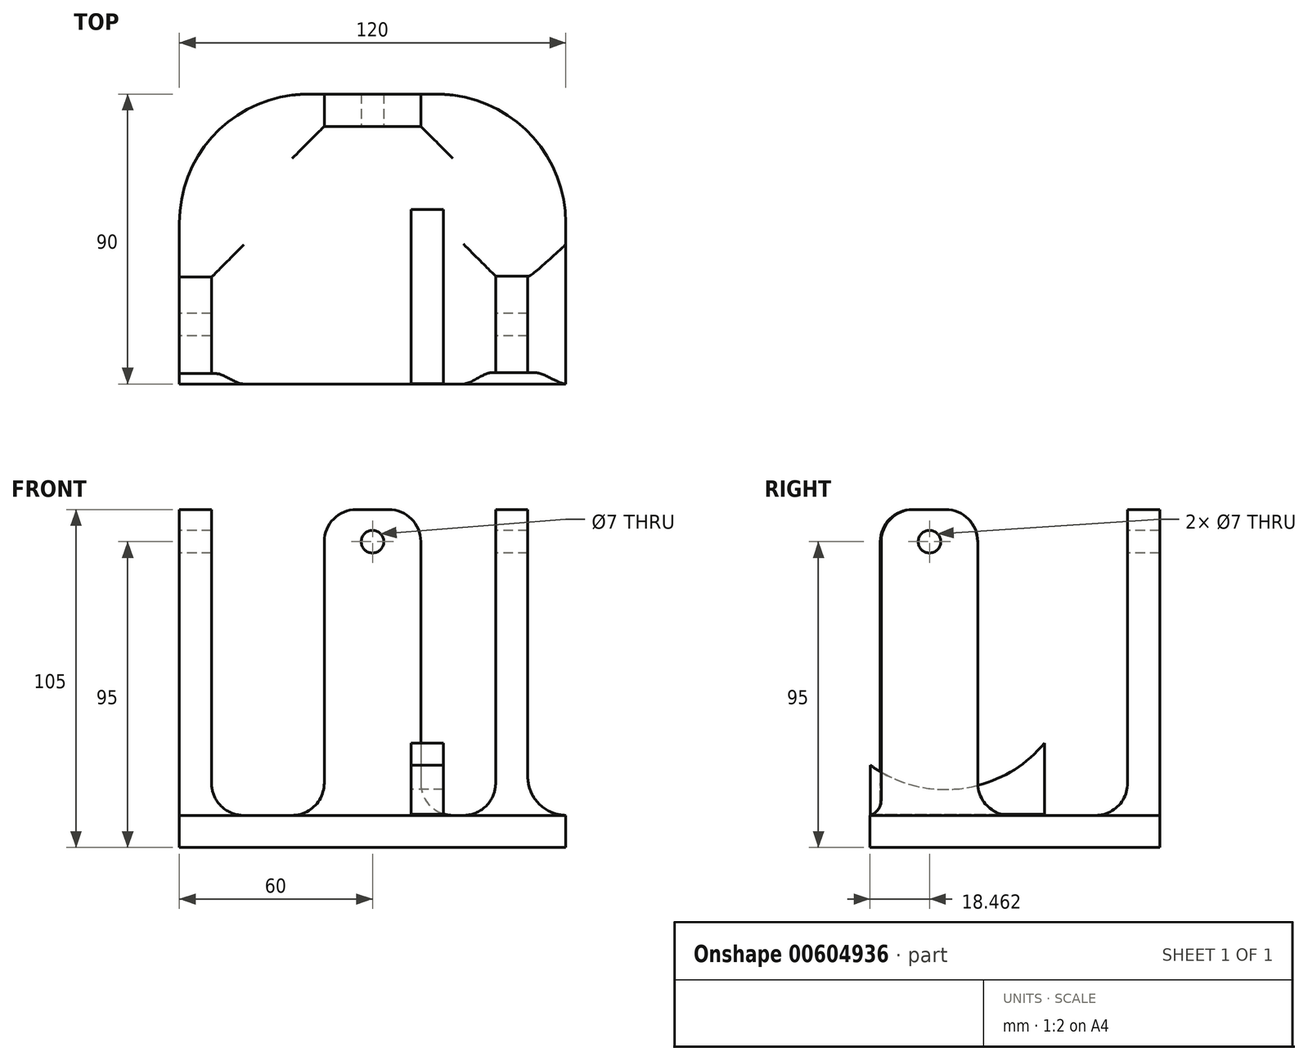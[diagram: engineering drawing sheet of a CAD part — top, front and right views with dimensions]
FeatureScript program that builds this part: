
annotation { "Feature Type Name" : "Feature", "Feature Type Description" : "" }
export const myFeature = defineFeature(function(context is Context, id is Id, definition is map)
    precondition{}
    {
        {
            var Q0;
            Q0=qCreatedBy(makeId("Top.planeOp"),FACE);
            var sketch = newSketch(context, id + "F0", { "sketchPlane" : qUnion([Q0])});
            skLineSegment(sketch, "E0.bottom", {"start": v(-20, 45) * mm, "end": v(20, 45) * mm});
            skLineSegment(sketch, "E0.top", {"start": v(-60, -45) * mm, "end": v(60, -45) * mm});
            skLineSegment(sketch, "E0.left", {"start": v(-60, 5) * mm, "end": v(-60, -45) * mm});
            skLineSegment(sketch, "E0.right", {"start": v(60, 5) * mm, "end": v(60, -45) * mm});
            skPoint(sketch, "E0.middle", {"position": v(0, 0) * mm});
            skPoint(sketch, "E1.visualSharp", {"position": v(-60, 45) * mm});
            skArc(sketch, "E1.filletArc", {"start": v(-20, 45) * mm, "mid": v(-48.28, 33.28) * mm, "end": v(-60, 5) * mm});
            skPoint(sketch, "E2.visualSharp", {"position": v(60, 45) * mm});
            skArc(sketch, "E2.filletArc", {"start": v(60, 5) * mm, "mid": v(48.28, 33.28) * mm, "end": v(20, 45) * mm});
            skSolve(sketch);
        }
        {
            var Q0;
            Q0=makeQuery(id+"F0.imprint","IMPRINT",FACE,{"disambiguationData":[TD([[makeQuery(id+"F0.imprint","IMPRINT",EDGE,{"derivedFrom":sQuery(id+"F0.wireOp",EDGE,"E0.bottom")}),-1.0]])]});
            extrude(context, id + "F1", {"entities" : qUnion([Q0]), "depth" : 10 * mm, "offsetDistance" : 25 * mm});
        }
        {
            var Q0;
            Q0=makeQuery(id+"F1.opExtrude","CAP_FACE",FACE,{"disambiguationData":[OSD([sQuery(id+"F0.wireOp",EDGE,"E0.bottom"),sQuery(id+"F0.wireOp",EDGE,"E0.top"),sQuery(id+"F0.wireOp",EDGE,"E0.left"),sQuery(id+"F0.wireOp",EDGE,"E0.right"),sQuery(id+"F0.wireOp",EDGE,"E1.filletArc"),sQuery(id+"F0.wireOp",EDGE,"E2.filletArc")])],"isStart":false});
            var sketch = newSketch(context, id + "F2", { "sketchPlane" : qUnion([Q0])});
            skSolve(sketch);
        }
        {
            var Q0;
            Q0=qCreatedBy(makeId("Top.planeOp"),FACE);
            var sketch = newSketch(context, id + "F3", { "sketchPlane" : qUnion([Q0])});
            skLineSegment(sketch, "E3.bottom", {"start": v(-60, -41.81) * mm, "end": v(-50, -41.81) * mm});
            skLineSegment(sketch, "E3.top", {"start": v(-60, -11.81) * mm, "end": v(-50, -11.81) * mm});
            skLineSegment(sketch, "E3.left", {"start": v(-60, -41.81) * mm, "end": v(-60, -11.81) * mm});
            skLineSegment(sketch, "E3.right", {"start": v(-50, -41.81) * mm, "end": v(-50, -11.81) * mm});
            skLineSegment(sketch, "E4.bottom", {"start": v(38.23, -41.54) * mm, "end": v(48.23, -41.54) * mm});
            skLineSegment(sketch, "E4.top", {"start": v(38.23, -11.54) * mm, "end": v(48.23, -11.54) * mm});
            skLineSegment(sketch, "E4.left", {"start": v(38.23, -41.54) * mm, "end": v(38.23, -11.54) * mm});
            skLineSegment(sketch, "E4.right", {"start": v(48.23, -41.54) * mm, "end": v(48.23, -11.54) * mm});
            skLineSegment(sketch, "E5.bottom", {"start": v(-15, 45) * mm, "end": v(15, 45) * mm});
            skLineSegment(sketch, "E5.top", {"start": v(-15, 35) * mm, "end": v(15, 35) * mm});
            skLineSegment(sketch, "E5.left", {"start": v(-15, 45) * mm, "end": v(-15, 35) * mm});
            skLineSegment(sketch, "E5.right", {"start": v(15, 45) * mm, "end": v(15, 35) * mm});
            skSolve(sketch);
        }
        {
            var Q0;
            Q0 = qSketchRegion(id + "F3", true);
            extrude(context, id + "F4", {"entities" : qUnion([Q0]), "operationType" : NewBodyOperationType.ADD, "depth" : 25 * mm, "offsetDistance" : 25 * mm});
        }
        {
            var Q0;
            Q0 = qSketchRegion(id + "F3", true);
            var Q1;
            Q1=makeQuery(id+"F4.opExtrude","CAP_FACE",FACE,{"disambiguationData":[OSD([sQuery(id+"F3.wireOp",EDGE,"E3.bottom"),sQuery(id+"F3.wireOp",EDGE,"E3.top"),sQuery(id+"F3.wireOp",EDGE,"E3.left"),sQuery(id+"F3.wireOp",EDGE,"E3.right")])],"isStart":false});
            var Q2;
            Q2=makeQuery(id+"F4.opExtrude","CAP_FACE",FACE,{"disambiguationData":[OSD([sQuery(id+"F3.wireOp",EDGE,"E5.bottom"),sQuery(id+"F3.wireOp",EDGE,"E5.top"),sQuery(id+"F3.wireOp",EDGE,"E5.left"),sQuery(id+"F3.wireOp",EDGE,"E5.right")])],"isStart":false});
            var Q3;
            Q3=makeQuery(id+"F4.opExtrude","CAP_FACE",FACE,{"disambiguationData":[OSD([sQuery(id+"F3.wireOp",EDGE,"E4.bottom"),sQuery(id+"F3.wireOp",EDGE,"E4.top"),sQuery(id+"F3.wireOp",EDGE,"E4.left"),sQuery(id+"F3.wireOp",EDGE,"E4.right")])],"isStart":false});
            extrude(context, id + "F5", {"entities" : qUnion([Q0, Q1, Q2, Q3]), "operationType" : NewBodyOperationType.ADD, "depth" : 80 * mm, "offsetDistance" : 25 * mm});
        }
        {
            var Q0;
            {var subQ0=sQuery(id+"F3.wireOp",EDGE,"E4.bottom");Q0=makeQuery(id+"F5.opExtrude","CAP_EDGE",EDGE,{"disambiguationData":[OSD([subQ0]),TDD([makeQuery(id+"F4.opExtrude","CAP_EDGE",EDGE,{"disambiguationData":[OSD([subQ0])],"isStart":false})])],"isStart":false});}
            var Q1;
            {var subQ0=sQuery(id+"F3.wireOp",EDGE,"E4.top");Q1=makeQuery(id+"F5.opExtrude","CAP_EDGE",EDGE,{"disambiguationData":[OSD([subQ0]),TDD([makeQuery(id+"F4.opExtrude","CAP_EDGE",EDGE,{"disambiguationData":[OSD([subQ0])],"isStart":false})])],"isStart":false});}
            fillet(context, id + "F6", {"entities" : qUnion([Q0, Q1]), "radius" : 10 * mm, "tangentPropagation" : true, "allowEdgeOverflow" : false});
        }
        {
            var Q0;
            {var subQ0=sQuery(id+"F3.wireOp",EDGE,"E5.right");Q0=makeQuery(id+"F5.opExtrude","CAP_EDGE",EDGE,{"disambiguationData":[OSD([subQ0]),TDD([makeQuery(id+"F4.opExtrude","CAP_EDGE",EDGE,{"disambiguationData":[OSD([subQ0])],"isStart":false})])],"isStart":false});}
            fillet(context, id + "F7", {"entities" : qUnion([Q0]), "radius" : 10 * mm, "tangentPropagation" : true, "allowEdgeOverflow" : false});
        }
        {
            var Q0;
            {var subQ0=sQuery(id+"F3.wireOp",EDGE,"E5.left");Q0=makeQuery(id+"F5.opExtrude","CAP_EDGE",EDGE,{"disambiguationData":[OSD([subQ0]),TDD([makeQuery(id+"F4.opExtrude","CAP_EDGE",EDGE,{"disambiguationData":[OSD([subQ0])],"isStart":false})])],"isStart":false});}
            fillet(context, id + "F8", {"entities" : qUnion([Q0]), "radius" : 10 * mm, "tangentPropagation" : true, "allowEdgeOverflow" : false});
        }
        {
            var Q0;
            {var subQ0=sQuery(id+"F3.wireOp",EDGE,"E3.top");Q0=makeQuery(id+"F5.opExtrude","CAP_EDGE",EDGE,{"disambiguationData":[OSD([subQ0]),TDD([makeQuery(id+"F4.opExtrude","CAP_EDGE",EDGE,{"disambiguationData":[OSD([subQ0])],"isStart":false})])],"isStart":false});}
            var Q1;
            {var subQ0=sQuery(id+"F3.wireOp",EDGE,"E3.bottom");Q1=makeQuery(id+"F5.opExtrude","CAP_EDGE",EDGE,{"disambiguationData":[OSD([subQ0]),TDD([makeQuery(id+"F4.opExtrude","CAP_EDGE",EDGE,{"disambiguationData":[OSD([subQ0])],"isStart":false})])],"isStart":false});}
            fillet(context, id + "F9", {"entities" : qUnion([Q0, Q1]), "radius" : 10 * mm, "tangentPropagation" : true, "allowEdgeOverflow" : false});
        }
        {
            var Q0;
            {var subQ0=sQuery(id+"F3.wireOp",EDGE,"E5.top");Q0=makeQuery(id+"F5.boolean.opBoolean","MERGE",FACE,{"derivedFrom":[makeQuery(id+"F4.opExtrude","SWEPT_FACE",FACE,{"disambiguationData":[OSD([subQ0])]}),makeQuery(id+"F5.opExtrude","SWEPT_FACE",FACE,{"disambiguationData":[OSD([subQ0]),TDD([makeQuery(id+"F3.imprint","IMPRINT",EDGE,{"derivedFrom":subQ0})])]}),makeQuery(id+"F5.opExtrude","SWEPT_FACE",FACE,{"disambiguationData":[OSD([subQ0]),TDD([makeQuery(id+"F4.opExtrude","CAP_EDGE",EDGE,{"disambiguationData":[OSD([subQ0])],"isStart":false})])]})]});}
            var sketch = newSketch(context, id + "F10", { "sketchPlane" : qUnion([Q0])});
            skCircle(sketch, "E6", {"center": v(0, 95) * mm, "radius": 3.5 * mm});
            skSolve(sketch);
        }
        {
            var Q0;
            Q0=sQuery(id+"F10.wireOp",VERTEX,"E6.center");
            var Q1;
            Q1=makeQuery(id+"F1.opExtrude","SWEPT_BODY",BODY,{"disambiguationData":[OSD([sQuery(id+"F0.wireOp",EDGE,"E0.bottom"),sQuery(id+"F0.wireOp",EDGE,"E0.top"),sQuery(id+"F0.wireOp",EDGE,"E0.left"),sQuery(id+"F0.wireOp",EDGE,"E0.right"),sQuery(id+"F0.wireOp",EDGE,"E1.filletArc"),sQuery(id+"F0.wireOp",EDGE,"E2.filletArc")])]});
            hole(context, id + "F11", {"style" : HoleStyle.SIMPLE, "endStyle" : HoleEndStyle.THROUGH, "holeDiameter" : 7 * mm, "majorDiameter" : 5 * mm, "isTappedThrough" : true, "tappedDepth" : 12 * mm, "tapClearance" : 3, "locations" : qUnion([Q0]), "scope" : qUnion([Q1])});
        }
        {
            var Q0;
            {var subQ0=sQuery(id+"F3.wireOp",EDGE,"E3.left");Q0=makeQuery(id+"F5.boolean.opBoolean","MERGE",FACE,{"derivedFrom":[makeQuery(id+"F4.boolean.opBoolean","MERGE",FACE,{"derivedFrom":[makeQuery(id+"F1.opExtrude","SWEPT_FACE",FACE,{"disambiguationData":[OSD([sQuery(id+"F0.wireOp",EDGE,"E0.left")])]}),makeQuery(id+"F4.opExtrude","SWEPT_FACE",FACE,{"disambiguationData":[OSD([subQ0])]})]}),makeQuery(id+"F5.opExtrude","SWEPT_FACE",FACE,{"disambiguationData":[OSD([subQ0]),TDD([makeQuery(id+"F3.imprint","IMPRINT",EDGE,{"derivedFrom":subQ0})])]}),makeQuery(id+"F5.opExtrude","SWEPT_FACE",FACE,{"disambiguationData":[OSD([subQ0]),TDD([makeQuery(id+"F4.opExtrude","CAP_EDGE",EDGE,{"disambiguationData":[OSD([subQ0])],"isStart":false})])]})]});}
            var sketch = newSketch(context, id + "F12", { "sketchPlane" : qUnion([Q0])});
            skCircle(sketch, "E7", {"center": v(26.54, 95) * mm, "radius": 3.5 * mm});
            skSolve(sketch);
        }
        {
            var Q0;
            Q0=sQuery(id+"F12.wireOp",VERTEX,"E7.center");
            var Q1;
            Q1=makeQuery(id+"F1.opExtrude","SWEPT_BODY",BODY,{"disambiguationData":[OSD([sQuery(id+"F0.wireOp",EDGE,"E0.bottom"),sQuery(id+"F0.wireOp",EDGE,"E0.top"),sQuery(id+"F0.wireOp",EDGE,"E0.left"),sQuery(id+"F0.wireOp",EDGE,"E0.right"),sQuery(id+"F0.wireOp",EDGE,"E1.filletArc"),sQuery(id+"F0.wireOp",EDGE,"E2.filletArc")])]});
            hole(context, id + "F13", {"style" : HoleStyle.SIMPLE, "endStyle" : HoleEndStyle.THROUGH, "holeDiameter" : 7 * mm, "majorDiameter" : 5 * mm, "isTappedThrough" : true, "tappedDepth" : 12 * mm, "tapClearance" : 3, "locations" : qUnion([Q0]), "scope" : qUnion([Q1])});
        }
        {
            var Q0;
            Q0=makeQuery(id+"F4.boolean.opBoolean","INTERSECT",EDGE,{"derivedFrom":[makeQuery(id+"F1.opExtrude","CAP_FACE",FACE,{"disambiguationData":[OSD([sQuery(id+"F0.wireOp",EDGE,"E0.bottom"),sQuery(id+"F0.wireOp",EDGE,"E0.top"),sQuery(id+"F0.wireOp",EDGE,"E0.left"),sQuery(id+"F0.wireOp",EDGE,"E0.right"),sQuery(id+"F0.wireOp",EDGE,"E1.filletArc"),sQuery(id+"F0.wireOp",EDGE,"E2.filletArc")])],"isStart":false}),makeQuery(id+"F4.opExtrude","SWEPT_FACE",FACE,{"disambiguationData":[OSD([sQuery(id+"F3.wireOp",EDGE,"E3.top")])]})]});
            fillet(context, id + "F14", {"entities" : qUnion([Q0]), "radius" : 10 * mm, "tangentPropagation" : true, "allowEdgeOverflow" : false});
        }
        {
            var Q0;
            Q0=makeQuery(id+"F4.boolean.opBoolean","INTERSECT",EDGE,{"derivedFrom":[makeQuery(id+"F1.opExtrude","CAP_FACE",FACE,{"disambiguationData":[OSD([sQuery(id+"F0.wireOp",EDGE,"E0.bottom"),sQuery(id+"F0.wireOp",EDGE,"E0.top"),sQuery(id+"F0.wireOp",EDGE,"E0.left"),sQuery(id+"F0.wireOp",EDGE,"E0.right"),sQuery(id+"F0.wireOp",EDGE,"E1.filletArc"),sQuery(id+"F0.wireOp",EDGE,"E2.filletArc")])],"isStart":false}),makeQuery(id+"F4.opExtrude","SWEPT_FACE",FACE,{"disambiguationData":[OSD([sQuery(id+"F3.wireOp",EDGE,"E5.left")])]})]});
            fillet(context, id + "F15", {"entities" : qUnion([Q0]), "radius" : 10 * mm, "tangentPropagation" : true, "allowEdgeOverflow" : false});
        }
        {
            var Q0;
            Q0=makeQuery(id+"F4.boolean.opBoolean","INTERSECT",EDGE,{"derivedFrom":[makeQuery(id+"F1.opExtrude","CAP_FACE",FACE,{"disambiguationData":[OSD([sQuery(id+"F0.wireOp",EDGE,"E0.bottom"),sQuery(id+"F0.wireOp",EDGE,"E0.top"),sQuery(id+"F0.wireOp",EDGE,"E0.left"),sQuery(id+"F0.wireOp",EDGE,"E0.right"),sQuery(id+"F0.wireOp",EDGE,"E1.filletArc"),sQuery(id+"F0.wireOp",EDGE,"E2.filletArc")])],"isStart":false}),makeQuery(id+"F4.opExtrude","SWEPT_FACE",FACE,{"disambiguationData":[OSD([sQuery(id+"F3.wireOp",EDGE,"E5.right")])]})]});
            var Q1;
            Q1=makeQuery(id+"F4.boolean.opBoolean","INTERSECT",EDGE,{"derivedFrom":[makeQuery(id+"F1.opExtrude","CAP_FACE",FACE,{"disambiguationData":[OSD([sQuery(id+"F0.wireOp",EDGE,"E0.bottom"),sQuery(id+"F0.wireOp",EDGE,"E0.top"),sQuery(id+"F0.wireOp",EDGE,"E0.left"),sQuery(id+"F0.wireOp",EDGE,"E0.right"),sQuery(id+"F0.wireOp",EDGE,"E1.filletArc"),sQuery(id+"F0.wireOp",EDGE,"E2.filletArc")])],"isStart":false}),makeQuery(id+"F4.opExtrude","SWEPT_FACE",FACE,{"disambiguationData":[OSD([sQuery(id+"F3.wireOp",EDGE,"E4.top")])]})]});
            fillet(context, id + "F16", {"entities" : qUnion([Q0, Q1]), "radius" : 10 * mm, "tangentPropagation" : true, "allowEdgeOverflow" : false});
        }
        {
            var Q0;
            Q0=makeQuery(id+"F4.boolean.opBoolean","INTERSECT",EDGE,{"derivedFrom":[makeQuery(id+"F1.opExtrude","CAP_FACE",FACE,{"disambiguationData":[OSD([sQuery(id+"F0.wireOp",EDGE,"E0.bottom"),sQuery(id+"F0.wireOp",EDGE,"E0.top"),sQuery(id+"F0.wireOp",EDGE,"E0.left"),sQuery(id+"F0.wireOp",EDGE,"E0.right"),sQuery(id+"F0.wireOp",EDGE,"E1.filletArc"),sQuery(id+"F0.wireOp",EDGE,"E2.filletArc")])],"isStart":false}),makeQuery(id+"F4.opExtrude","SWEPT_FACE",FACE,{"disambiguationData":[OSD([sQuery(id+"F3.wireOp",EDGE,"E4.right")])]})]});
            fillet(context, id + "F17", {"entities" : qUnion([Q0]), "radius" : 12 * mm, "tangentPropagation" : true, "allowEdgeOverflow" : false});
        }
        {
            var Q0;
            Q0=makeQuery(id+"F4.boolean.opBoolean","INTERSECT",EDGE,{"derivedFrom":[makeQuery(id+"F1.opExtrude","CAP_FACE",FACE,{"disambiguationData":[OSD([sQuery(id+"F0.wireOp",EDGE,"E0.bottom"),sQuery(id+"F0.wireOp",EDGE,"E0.top"),sQuery(id+"F0.wireOp",EDGE,"E0.left"),sQuery(id+"F0.wireOp",EDGE,"E0.right"),sQuery(id+"F0.wireOp",EDGE,"E1.filletArc"),sQuery(id+"F0.wireOp",EDGE,"E2.filletArc")])],"isStart":false}),makeQuery(id+"F4.opExtrude","SWEPT_FACE",FACE,{"disambiguationData":[OSD([sQuery(id+"F3.wireOp",EDGE,"E4.bottom")])]})]});
            fillet(context, id + "F18", {"entities" : qUnion([Q0]), "radius" : 5 * mm, "tangentPropagation" : true, "allowEdgeOverflow" : false});
        }
        {
            var Q0;
            Q0=makeQuery(id+"F4.boolean.opBoolean","INTERSECT",EDGE,{"derivedFrom":[makeQuery(id+"F1.opExtrude","CAP_FACE",FACE,{"disambiguationData":[OSD([sQuery(id+"F0.wireOp",EDGE,"E0.bottom"),sQuery(id+"F0.wireOp",EDGE,"E0.top"),sQuery(id+"F0.wireOp",EDGE,"E0.left"),sQuery(id+"F0.wireOp",EDGE,"E0.right"),sQuery(id+"F0.wireOp",EDGE,"E1.filletArc"),sQuery(id+"F0.wireOp",EDGE,"E2.filletArc")])],"isStart":false}),makeQuery(id+"F4.opExtrude","SWEPT_FACE",FACE,{"disambiguationData":[OSD([sQuery(id+"F3.wireOp",EDGE,"E3.right")])]})]});
            fillet(context, id + "F19", {"entities" : qUnion([Q0]), "radius" : 10 * mm, "tangentPropagation" : true, "allowEdgeOverflow" : false});
        }
        {
            var Q0;
            Q0=makeQuery(id+"F4.boolean.opBoolean","INTERSECT",EDGE,{"derivedFrom":[makeQuery(id+"F1.opExtrude","CAP_FACE",FACE,{"disambiguationData":[OSD([sQuery(id+"F0.wireOp",EDGE,"E0.bottom"),sQuery(id+"F0.wireOp",EDGE,"E0.top"),sQuery(id+"F0.wireOp",EDGE,"E0.left"),sQuery(id+"F0.wireOp",EDGE,"E0.right"),sQuery(id+"F0.wireOp",EDGE,"E1.filletArc"),sQuery(id+"F0.wireOp",EDGE,"E2.filletArc")])],"isStart":false}),makeQuery(id+"F4.opExtrude","SWEPT_FACE",FACE,{"disambiguationData":[OSD([sQuery(id+"F3.wireOp",EDGE,"E3.bottom")])]})]});
            fillet(context, id + "F20", {"entities" : qUnion([Q0]), "radius" : 5 * mm, "tangentPropagation" : true, "allowEdgeOverflow" : false});
        }
        {
            var Q0;
            Q0=makeQuery(id+"F4.boolean.opBoolean","INTERSECT",EDGE,{"derivedFrom":[makeQuery(id+"F1.opExtrude","CAP_FACE",FACE,{"disambiguationData":[OSD([sQuery(id+"F0.wireOp",EDGE,"E0.bottom"),sQuery(id+"F0.wireOp",EDGE,"E0.top"),sQuery(id+"F0.wireOp",EDGE,"E0.left"),sQuery(id+"F0.wireOp",EDGE,"E0.right"),sQuery(id+"F0.wireOp",EDGE,"E1.filletArc"),sQuery(id+"F0.wireOp",EDGE,"E2.filletArc")])],"isStart":false}),makeQuery(id+"F4.opExtrude","SWEPT_FACE",FACE,{"disambiguationData":[OSD([sQuery(id+"F3.wireOp",EDGE,"E5.top")])]})]});
            fillet(context, id + "F21", {"entities" : qUnion([Q0]), "radius" : 10 * mm, "tangentPropagation" : true, "allowEdgeOverflow" : false});
        }
        {
            var Q0;
            Q0=makeQuery(id+"F4.boolean.opBoolean","INTERSECT",EDGE,{"derivedFrom":[makeQuery(id+"F1.opExtrude","CAP_FACE",FACE,{"disambiguationData":[OSD([sQuery(id+"F0.wireOp",EDGE,"E0.bottom"),sQuery(id+"F0.wireOp",EDGE,"E0.top"),sQuery(id+"F0.wireOp",EDGE,"E0.left"),sQuery(id+"F0.wireOp",EDGE,"E0.right"),sQuery(id+"F0.wireOp",EDGE,"E1.filletArc"),sQuery(id+"F0.wireOp",EDGE,"E2.filletArc")])],"isStart":false}),makeQuery(id+"F4.opExtrude","SWEPT_FACE",FACE,{"disambiguationData":[OSD([sQuery(id+"F3.wireOp",EDGE,"E4.left")])]})]});
            fillet(context, id + "F22", {"entities" : qUnion([Q0]), "radius" : 10 * mm, "tangentPropagation" : true, "allowEdgeOverflow" : false});
        }
        {
            var Q0;
            Q0=makeQuery(id+"F2.imprint","IMPRINT",FACE,{"disambiguationData":[TD([[makeQuery(id+"F2.imprint","IMPRINT",EDGE,{"derivedFrom":makeQuery(id+"F1.opExtrude","CAP_EDGE",EDGE,{"disambiguationData":[OSD([sQuery(id+"F0.wireOp",EDGE,"E0.bottom")])],"isStart":false})}),-1.0]])]});
            var sketch = newSketch(context, id + "F23", { "sketchPlane" : qUnion([Q0])});
            skLineSegment(sketch, "E8.bottom", {"start": v(11.98, -45) * mm, "end": v(21.98, -45) * mm});
            skLineSegment(sketch, "E8.top", {"start": v(11.98, 10) * mm, "end": v(21.98, 10) * mm});
            skLineSegment(sketch, "E8.left", {"start": v(11.98, -45) * mm, "end": v(11.98, 10) * mm});
            skLineSegment(sketch, "E8.right", {"start": v(21.98, -45) * mm, "end": v(21.98, 10) * mm});
            skSolve(sketch);
        }
        {
            var Q0;
            Q0=qCreatedBy(makeId("Right.planeOp"),FACE);
            cPlane(context, id + "F24", {"entities" : qUnion([Q0]), "cplaneType" : CPlaneType.OFFSET, "offset" : 12 * mm, "width" : 150 * mm, "height" : 150 * mm});
        }
        {
            var Q0;
            Q0=qCreatedBy(id+"F24.planeOp",FACE);
            var sketch = newSketch(context, id + "F25", { "sketchPlane" : qUnion([Q0])});
            skLineSegment(sketch, "E9", {"start": v(-44.9, 10.36) * mm, "end": v(-44.9, 25.6) * mm});
            skLineSegment(sketch, "E10", {"start": v(-44.9, 10.36) * mm, "end": v(9.18, 10.36) * mm});
            skLineSegment(sketch, "E11", {"start": v(9.18, 10.36) * mm, "end": v(9.18, 32.44) * mm});
            skArc(sketch, "E12", {"start": v(-44.9, 25.6) * mm, "mid": v(-16.51, 18.34) * mm, "end": v(9.18, 32.44) * mm});
            skSolve(sketch);
        }
        {
            var Q0;
            Q0=makeQuery(id+"F25.imprint","IMPRINT",FACE,{"disambiguationData":[TD([[makeQuery(id+"F25.imprint","IMPRINT",EDGE,{"derivedFrom":sQuery(id+"F25.wireOp",EDGE,"E9")}),-1.0]])]});
            extrude(context, id + "F26", {"entities" : qUnion([Q0]), "depth" : 10 * mm, "offsetDistance" : 25 * mm});
        }
    });
